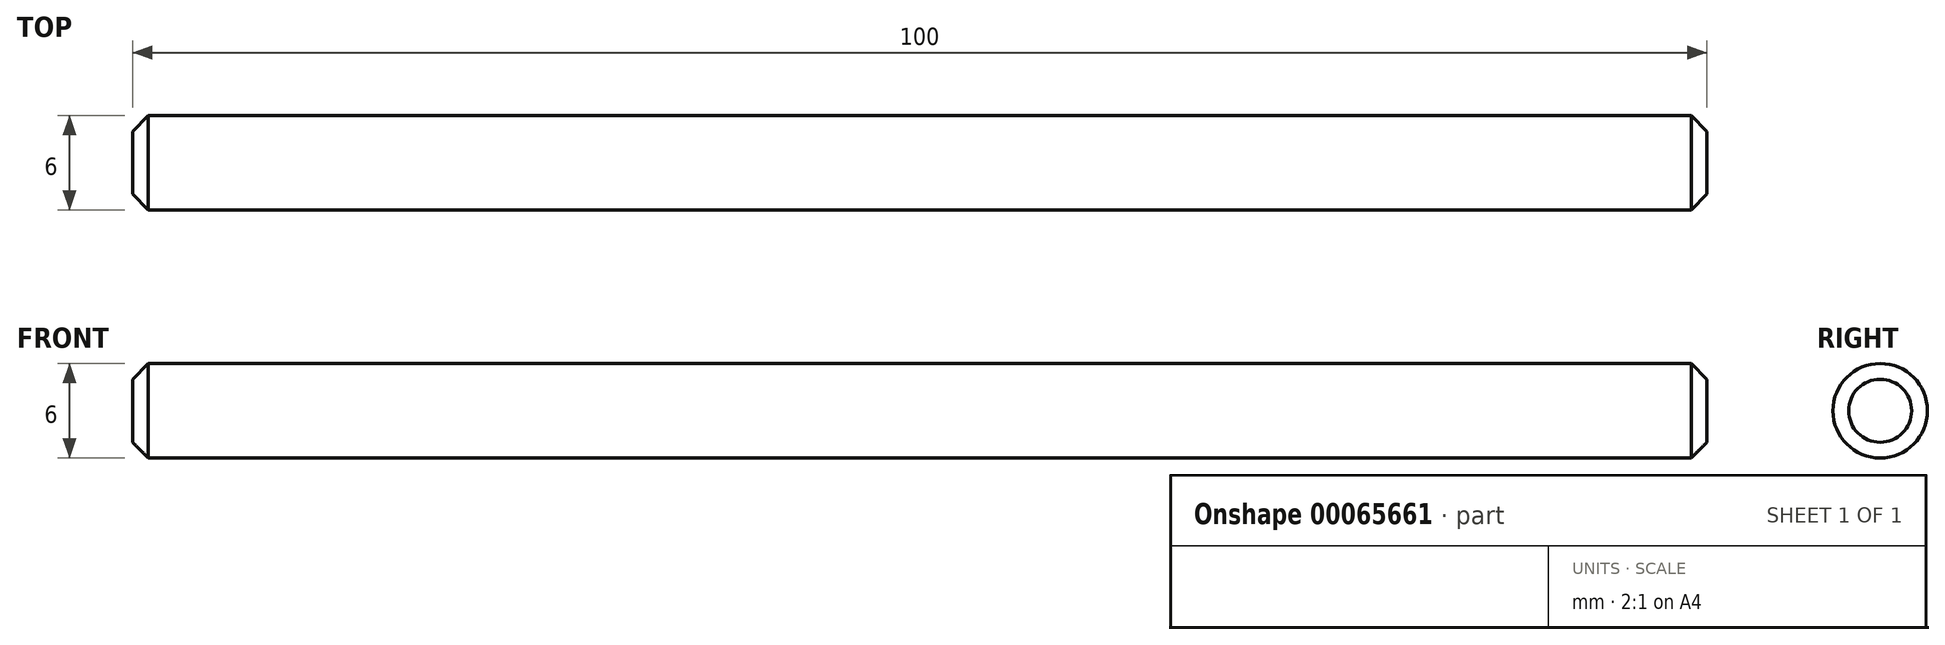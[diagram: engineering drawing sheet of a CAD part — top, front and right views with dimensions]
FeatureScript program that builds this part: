
annotation { "Feature Type Name" : "Feature", "Feature Type Description" : "" }
export const myFeature = defineFeature(function(context is Context, id is Id, definition is map)
    precondition{}
    {
        {
            var Q0;
            Q0=qCreatedBy(makeId("Right.planeOp"),FACE);
            var sketch = newSketch(context, id + "F0", { "sketchPlane" : qUnion([Q0])});
            skCircle(sketch, "E0", {"center": v(0, 0) * mm, "radius": 3 * mm});
            skSolve(sketch);
        }
        {
            var Q0;
            Q0 = qSketchRegion(id + "F0", true);
            extrude(context, id + "F1", {"entities" : qUnion([Q0]), "endBound" : BoundingType.SYMMETRIC, "depth" : 100 * mm});
        }
        {
            var Q0;
            Q0=makeQuery(id+"F1.opExtrude","CAP_EDGE",EDGE,{"disambiguationData":[OSD([sQuery(id+"F0.wireOp",EDGE,"E0")])],"isStart":false});
            var Q1;
            Q1=makeQuery(id+"F1.opExtrude","CAP_EDGE",EDGE,{"disambiguationData":[OSD([sQuery(id+"F0.wireOp",EDGE,"E0")])],"isStart":true});
            chamfer(context, id + "F2", {"entities" : qUnion([Q0, Q1]), "width" : 1 * mm, "tangentPropagation" : true});
        }
    });
